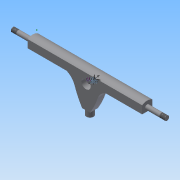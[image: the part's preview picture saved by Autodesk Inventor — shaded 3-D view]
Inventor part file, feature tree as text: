
AUTODESK INVENTOR PART (.ipt)
format: ipt  version: 2015 (Build 190159000, 159)  size: 146,432 bytes
history: native  units: in
note: dims shown in document units (in); Inventor stores cm internally (conversion verified against a paired STEP export)
features: extrude x5, sketch x5, plane x3, fillet x3, thread x2, mirror x1
ambient origin geometry x8: Origin, YZ Plane, XZ Plane, XY Plane, X Axis, Y Axis, Z Axis, Center Point
bodies: Solid1 (feature_tree)
feature tree (19):
  extrude  "Truck Axle"  Depth=0.71in
  extrude  "Axle"  Depth=1.375in TaperAngle=0.0deg
  plane  "Work Plane1"
  mirror  "Other Axle"
  plane  "Work Plane3"
  extrude  "Pentagon"  Depth=1.0in
  fillet  "Fillet1"  Radius=1.0in
  extrude  "Inner hole"  Depth=0.4in TaperAngle=0.0deg
  extrude  "Ball joint"  Depth=1.0in
  fillet  "Fillet3"  Radius=0.375in
  thread  "Thread3"  [1 undecoded]
  thread  "Thread4"  [1 undecoded]
  fillet  "Fillet6"  Radius=1.8in
  sketch  "Sketch1"  dims[d0=0.55in d1=0.71in]
  sketch  "Sketch2"  dims[d6=8.0in d7=0.0in d8=1.375in d9=0.0in]
  plane  "Work Plane2"
  sketch  "Sketch4"  dims[d19=0.5512in d20=0.0in d25=0.55in d29=1.0in]
  sketch  "Sketch6"  dims[d31=2.0in d32=0.0in d37=0.4in d38=0.0in]
  sketch  "Sketch10"  dims[d39=0.05in d40=0.3125in d41=0.375in d42=0.0in d43=0.375in d44=0.0in d45=0.5in d49=1.8in d50=1.5in d53=5.0in d54=0.65in d56=1.0in d57=1.1811in]
note: 2 required parameter values undecoded (feature->parameter linkage not recoverable at this tier; creation-order binding heuristic only, values carry confidence <= 0.55)
